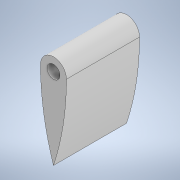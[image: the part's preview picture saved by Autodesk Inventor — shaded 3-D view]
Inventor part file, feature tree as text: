
AUTODESK INVENTOR PART (.ipt)
format: ipt  version: 2022 (Build 260153000, 153)  size: 101,888 bytes
history: native  units: mm
features: sketch x2, extrude x1, hole x1
ambient origin geometry x8: Origin, YZ Plane, XZ Plane, XY Plane, X Axis, Y Axis, Z Axis, Center Point
bodies: Solid1 (feature_tree)
feature tree (4):
  extrude  "Extrusion1"  Depth=8.0mm
  hole  "Hole1"  [1 undecoded]
  sketch  "Sketch1"  dims[d0=8.0mm d2=50.0mm]
  sketch  "Sketch2"  dims[d3=45.0mm d4=0.0mm d5=8.0mm d6=6.0mm d7=4.0mm d8=2.0mm d9=90.0deg d10=8.0mm d11=20.594885mm]
note: 1 required parameter value undecoded (feature->parameter linkage not recoverable at this tier; creation-order binding heuristic only, values carry confidence <= 0.55)
